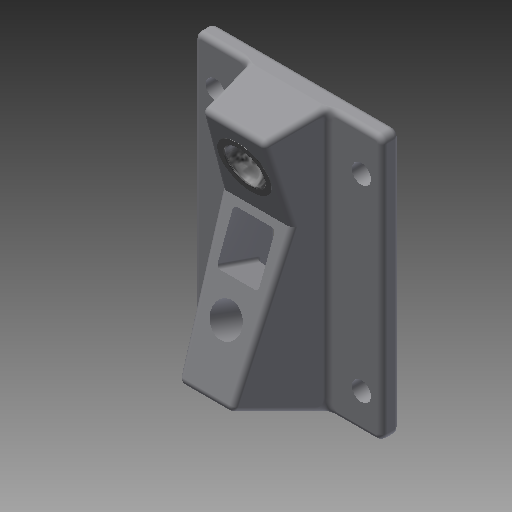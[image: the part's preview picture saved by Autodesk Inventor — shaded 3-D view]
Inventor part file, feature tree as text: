
AUTODESK INVENTOR PART (.ipt)
format: ipt  version: 2019 (Build 230136000, 136)  size: 590,336 bytes
history: native  units: mm
features: sketch x7, extrude x6, other x4, fillet x3, loft x2, hole x1, revolve x1
ambient origin geometry x8: Origin, YZ Plane, XZ Plane, XY Plane, X Axis, Y Axis, Z Axis, Center Point
bodies: Solido1 (feature_tree)
feature tree (24):
  extrude  "Estrusione1"  Depth=76.0mm
  extrude  "Estrusione2"  Depth=54.0mm
  extrude  "Estrusione3"  Depth=2.0mm
  extrude  "Estrusione4"  Depth=5.0mm TaperAngle=0.0deg
  fillet  "Raccordo1"  Radius=23.0mm
  sketch  "Schizzo5"
  loft  "Loft1"
  sketch  "Schizzo10"
  other  "Piano di lavoro1"
  loft  "Loft2"
  hole  "Foro1"  [1 undecoded]
  fillet  "Raccordo2"  Radius=10.0mm
  revolve  "Rivoluzione1"
  extrude  "Estrusione5"  Depth=24.0mm TaperAngle=0.0deg
  fillet  "Raccordo3"  Radius=15.0mm
  extrude  "Estrusione6"  Depth=46.0mm
  sketch  "Schizzo3"
  other  "Linea chiusa proiettata1"
  sketch  "Schizzo4"
  other  "Linea chiusa proiettata2"
  sketch  "Schizzo12"
  other  "Linea chiusa proiettata4"
  sketch  "Schizzo13"
  sketch  "Schizzo15"
note: 1 required parameter value undecoded (feature->parameter linkage not recoverable at this tier; creation-order binding heuristic only, values carry confidence <= 0.55)
